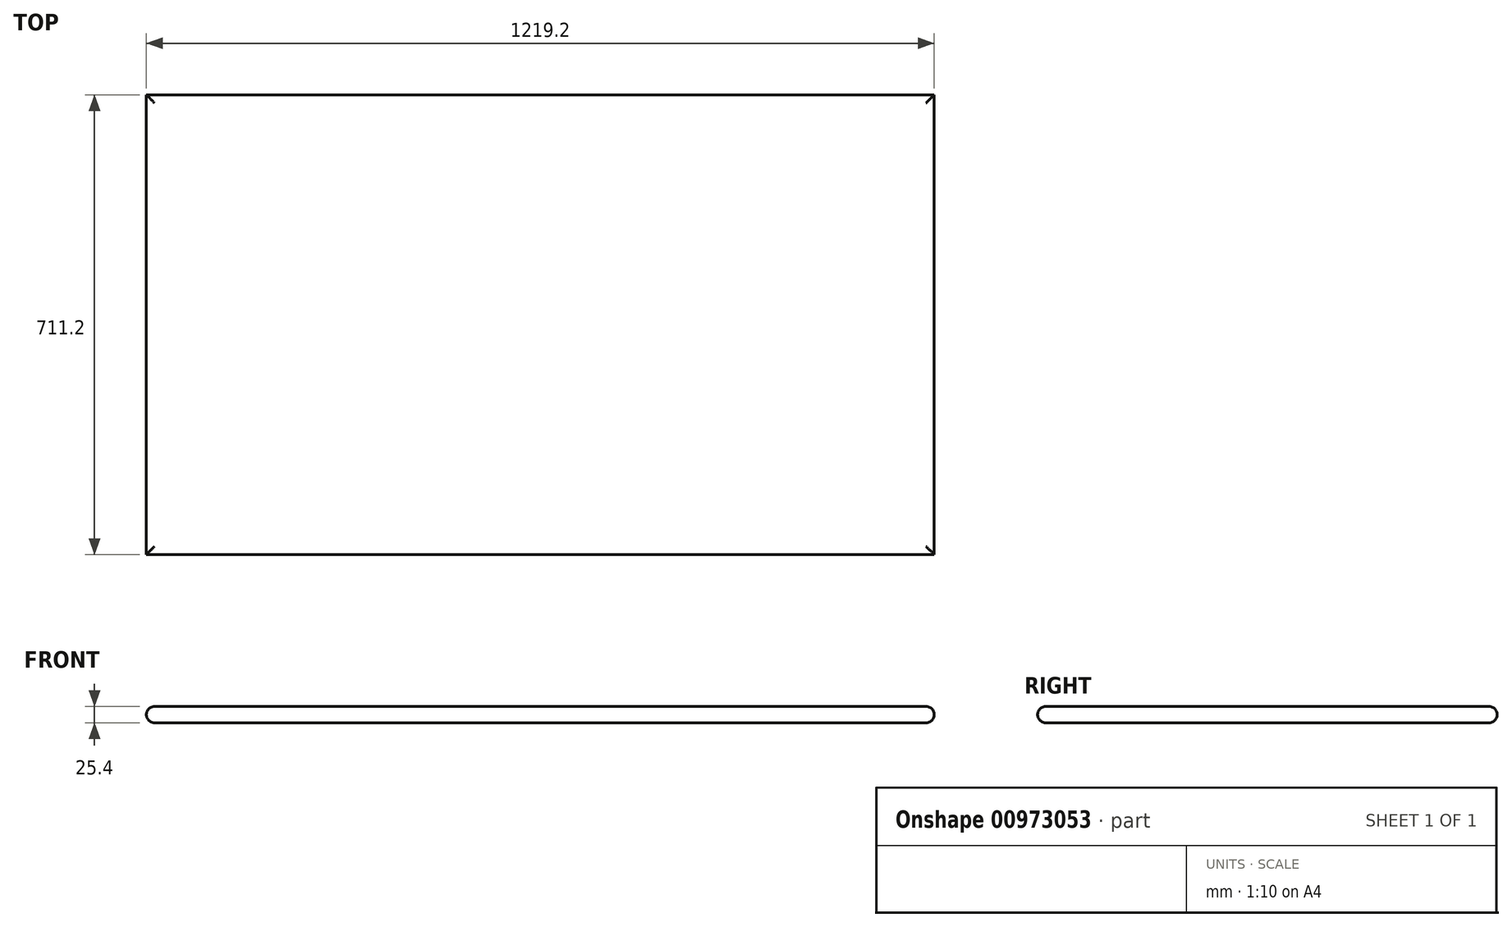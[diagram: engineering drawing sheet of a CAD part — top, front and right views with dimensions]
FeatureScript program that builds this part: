
annotation { "Feature Type Name" : "Feature", "Feature Type Description" : "" }
export const myFeature = defineFeature(function(context is Context, id is Id, definition is map)
    precondition{}
    {
        {
            var Q0;
            Q0=qCreatedBy(makeId("Top.planeOp"),FACE);
            var sketch = newSketch(context, id + "F0", { "sketchPlane" : qUnion([Q0])});
            skLineSegment(sketch, "E0.bottom", {"start": v(609.6, 355.6) * mm, "end": v(-609.6, 355.6) * mm});
            skLineSegment(sketch, "E0.top", {"start": v(609.6, -355.6) * mm, "end": v(-609.6, -355.6) * mm});
            skLineSegment(sketch, "E0.left", {"start": v(609.6, 355.6) * mm, "end": v(609.6, -355.6) * mm});
            skLineSegment(sketch, "E0.right", {"start": v(-609.6, 355.6) * mm, "end": v(-609.6, -355.6) * mm});
            skPoint(sketch, "E0.middle", {"position": v(0, 0) * mm});
            skSolve(sketch);
        }
        {
            var Q0;
            Q0=makeQuery(id+"F0.imprint","IMPRINT",FACE,{"disambiguationData":[TD([[makeQuery(id+"F0.imprint","IMPRINT",EDGE,{"derivedFrom":sQuery(id+"F0.wireOp",EDGE,"E0.bottom")}),1.0]])]});
            extrude(context, id + "F1", {"entities" : qUnion([Q0]), "depth" : 25.4 * mm, "offsetDistance" : 25.4 * mm});
        }
        {
            var Q0;
            Q0=makeQuery(id+"F1.opExtrude","CAP_FACE",FACE,{"disambiguationData":[OSD([sQuery(id+"F0.wireOp",EDGE,"E0.bottom"),sQuery(id+"F0.wireOp",EDGE,"E0.top"),sQuery(id+"F0.wireOp",EDGE,"E0.left"),sQuery(id+"F0.wireOp",EDGE,"E0.right")])],"isStart":false});
            var Q1;
            Q1=makeQuery(id+"F1.opExtrude","CAP_FACE",FACE,{"disambiguationData":[OSD([sQuery(id+"F0.wireOp",EDGE,"E0.bottom"),sQuery(id+"F0.wireOp",EDGE,"E0.top"),sQuery(id+"F0.wireOp",EDGE,"E0.left"),sQuery(id+"F0.wireOp",EDGE,"E0.right")])],"isStart":true});
            fillet(context, id + "F2", {"entities" : qUnion([Q0, Q1]), "radius" : 12.7 * mm, "tangentPropagation" : true, "allowEdgeOverflow" : false});
        }
    });
